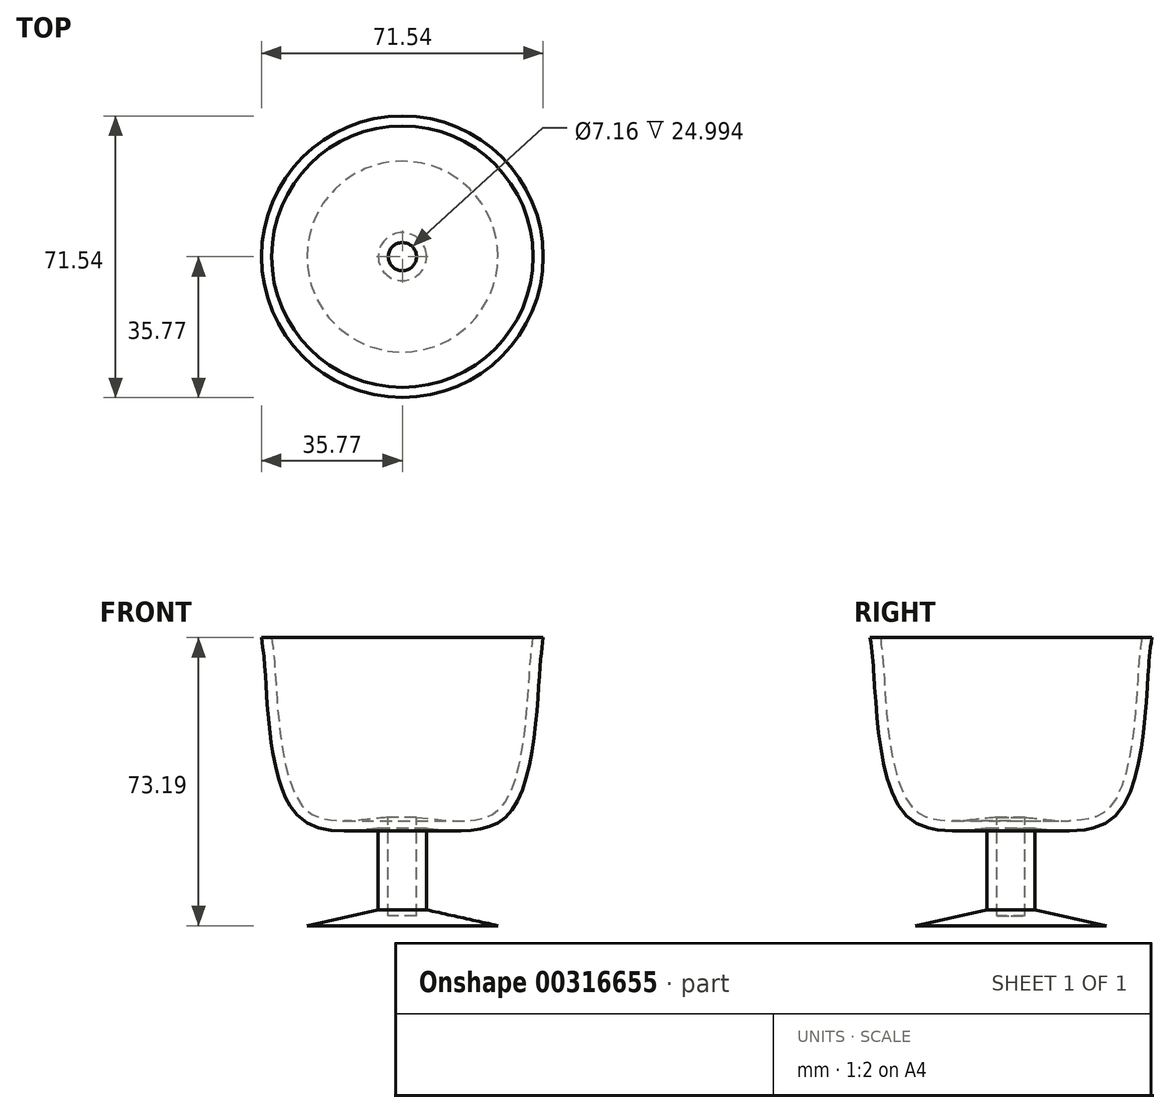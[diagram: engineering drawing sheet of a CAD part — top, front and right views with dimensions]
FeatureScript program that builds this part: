
annotation { "Feature Type Name" : "Feature", "Feature Type Description" : "" }
export const myFeature = defineFeature(function(context is Context, id is Id, definition is map)
    precondition{}
    {
        {
            var Q0;
            Q0=qCreatedBy(makeId("Front.planeOp"),FACE);
            var sketch = newSketch(context, id + "F0", { "sketchPlane" : qUnion([Q0])});
            skLineSegment(sketch, "E0", {"start": v(0, 0) * mm, "end": v(0, 76.48) * mm, "construction": true});
            skLineSegment(sketch, "E1", {"start": v(0, 0) * mm, "end": v(-24.24, 0) * mm});
            skLineSegment(sketch, "E2", {"start": v(-24.24, 0) * mm, "end": v(-6.12, 4) * mm});
            skLineSegment(sketch, "E3", {"start": v(-6.12, 4) * mm, "end": v(-6.12, 24.7) * mm});
            skFitSpline(sketch, "E4", {"points": [v(-6.12, 24.7) * mm, v(-27.3, 28.7) * mm, v(-34.83, 63.77) * mm, v(-35.77, 73.19) * mm], "startDerivative": vector(-72.4, -7.71) * mm, "endDerivative": vector(-4.14, 31.18) * mm});
            skLineSegment(sketch, "E5", {"start": v(-35.77, 73.19) * mm, "end": v(0, 73.19) * mm});
            skLineSegment(sketch, "E6", {"start": v(0, 73.19) * mm, "end": v(0, 0) * mm});
            skSolve(sketch);
        }
        {
            var Q0;
            Q0=makeQuery(id+"F0.imprint","IMPRINT",FACE,{"disambiguationData":[TD([[makeQuery(id+"F0.imprint","IMPRINT",EDGE,{"derivedFrom":sQuery(id+"F0.wireOp",EDGE,"E1")}),-1.0]])]});
            var Q1;
            Q1=sQuery(id+"F0.wireOp",EDGE,"E6");
            revolve(context, id + "F1", {"entities" : qUnion([Q0]), "axis" : qUnion([Q1]), "revolveType" : RevolveType.FULL});
        }
        {
            var Q0;
            Q0=makeQuery(id+"F1.opRevolve","SWEPT_FACE",FACE,{"disambiguationData":[OSD([sQuery(id+"F0.wireOp",EDGE,"E5")])]});
            shell(context, id + "F2", {"entities" : qUnion([Q0]), "thickness" : 2.54 * mm});
        }
    });
